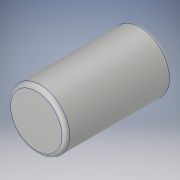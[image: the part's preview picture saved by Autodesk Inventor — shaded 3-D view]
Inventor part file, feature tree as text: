
AUTODESK INVENTOR PART (.ipt)
format: ipt  version: 2018 (Build 220112000, 112)  size: 113,664 bytes
history: native  units: in
note: dims shown in document units (in); Inventor stores cm internally (conversion verified against a paired STEP export)
features: extrude x1, fillet x1, sketch x1
ambient origin geometry x8: Origin, YZ Plane, XZ Plane, XY Plane, X Axis, Y Axis, Z Axis, Center Point
bodies: Solid1 (feature_tree)
feature tree (3):
  extrude  "Extrusion1"  Depth=0.14in TaperAngle=0.0deg
  fillet  "Fillet1"  Radius=0.005in
  sketch  "Sketch1"  dims[d0=0.077in d1=0.14in d2=0.0in d3=0.005in]
